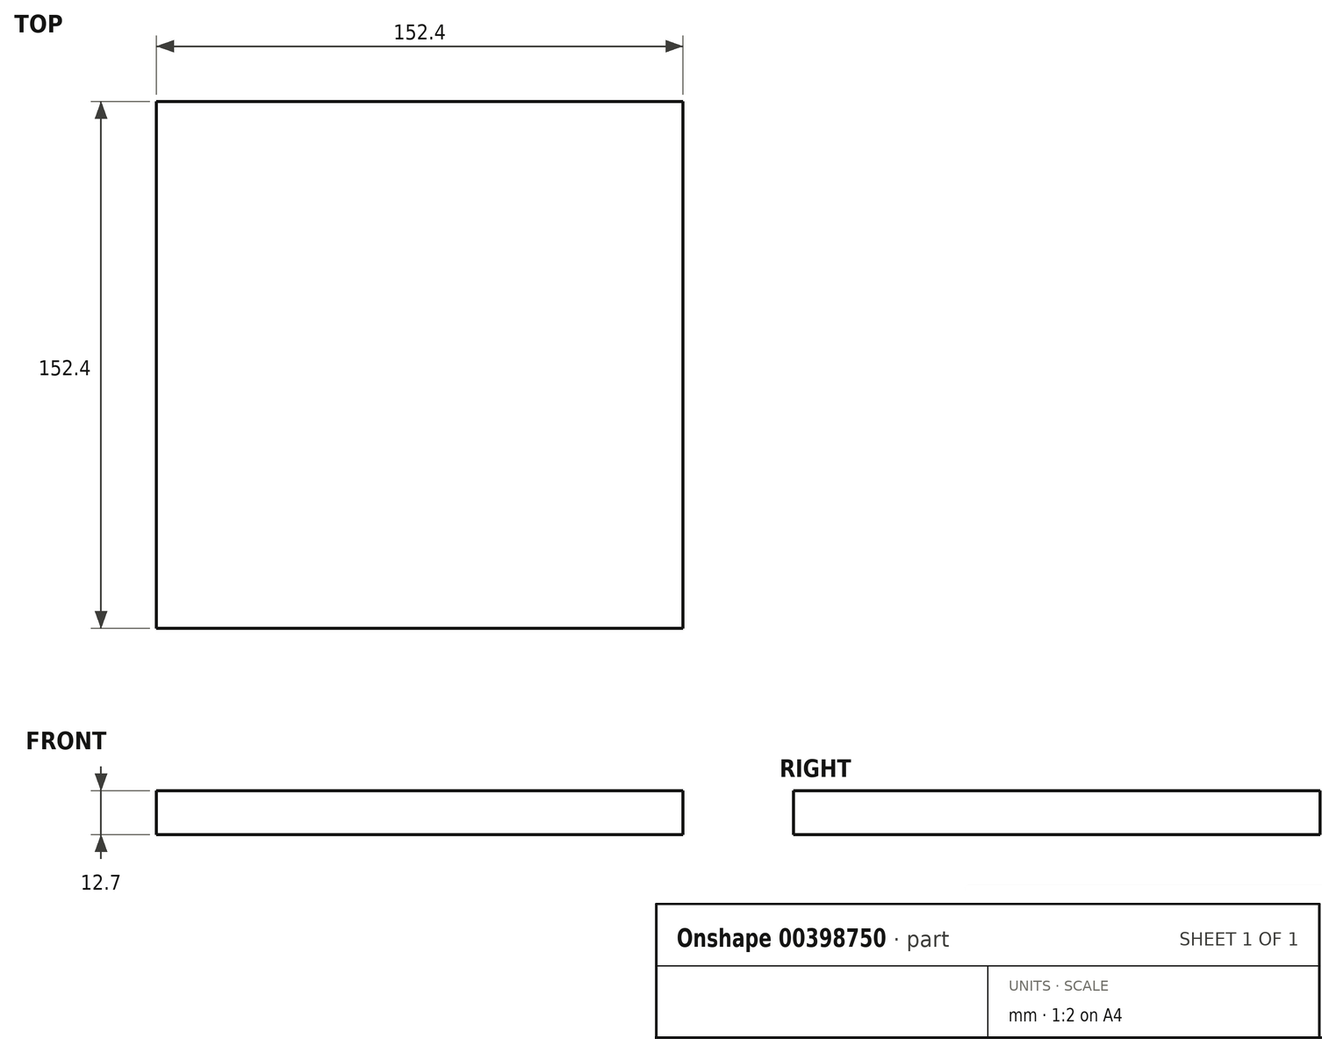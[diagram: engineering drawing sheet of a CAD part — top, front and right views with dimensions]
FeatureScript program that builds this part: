
annotation { "Feature Type Name" : "Feature", "Feature Type Description" : "" }
export const myFeature = defineFeature(function(context is Context, id is Id, definition is map)
    precondition{}
    {
        {
            var Q0;
            Q0=qCreatedBy(makeId("Top.planeOp"),FACE);
            var sketch = newSketch(context, id + "F0", { "sketchPlane" : qUnion([Q0])});
            skLineSegment(sketch, "E0.bottom", {"start": v(-94.45, 129.26) * mm, "end": v(57.95, 129.26) * mm});
            skLineSegment(sketch, "E0.top", {"start": v(-94.45, -23.14) * mm, "end": v(57.95, -23.14) * mm});
            skLineSegment(sketch, "E0.left", {"start": v(-94.45, 129.26) * mm, "end": v(-94.45, -23.14) * mm});
            skLineSegment(sketch, "E0.right", {"start": v(57.95, 129.26) * mm, "end": v(57.95, -23.14) * mm});
            skSolve(sketch);
        }
        {
            var Q0;
            Q0=makeQuery(id+"F0.imprint","IMPRINT",FACE,{"disambiguationData":[TD([[makeQuery(id+"F0.imprint","IMPRINT",EDGE,{"derivedFrom":sQuery(id+"F0.wireOp",EDGE,"E0.bottom")}),-1.0]])]});
            extrude(context, id + "F1", {"entities" : qUnion([Q0]), "depth" : 12.7 * mm});
        }
    });
